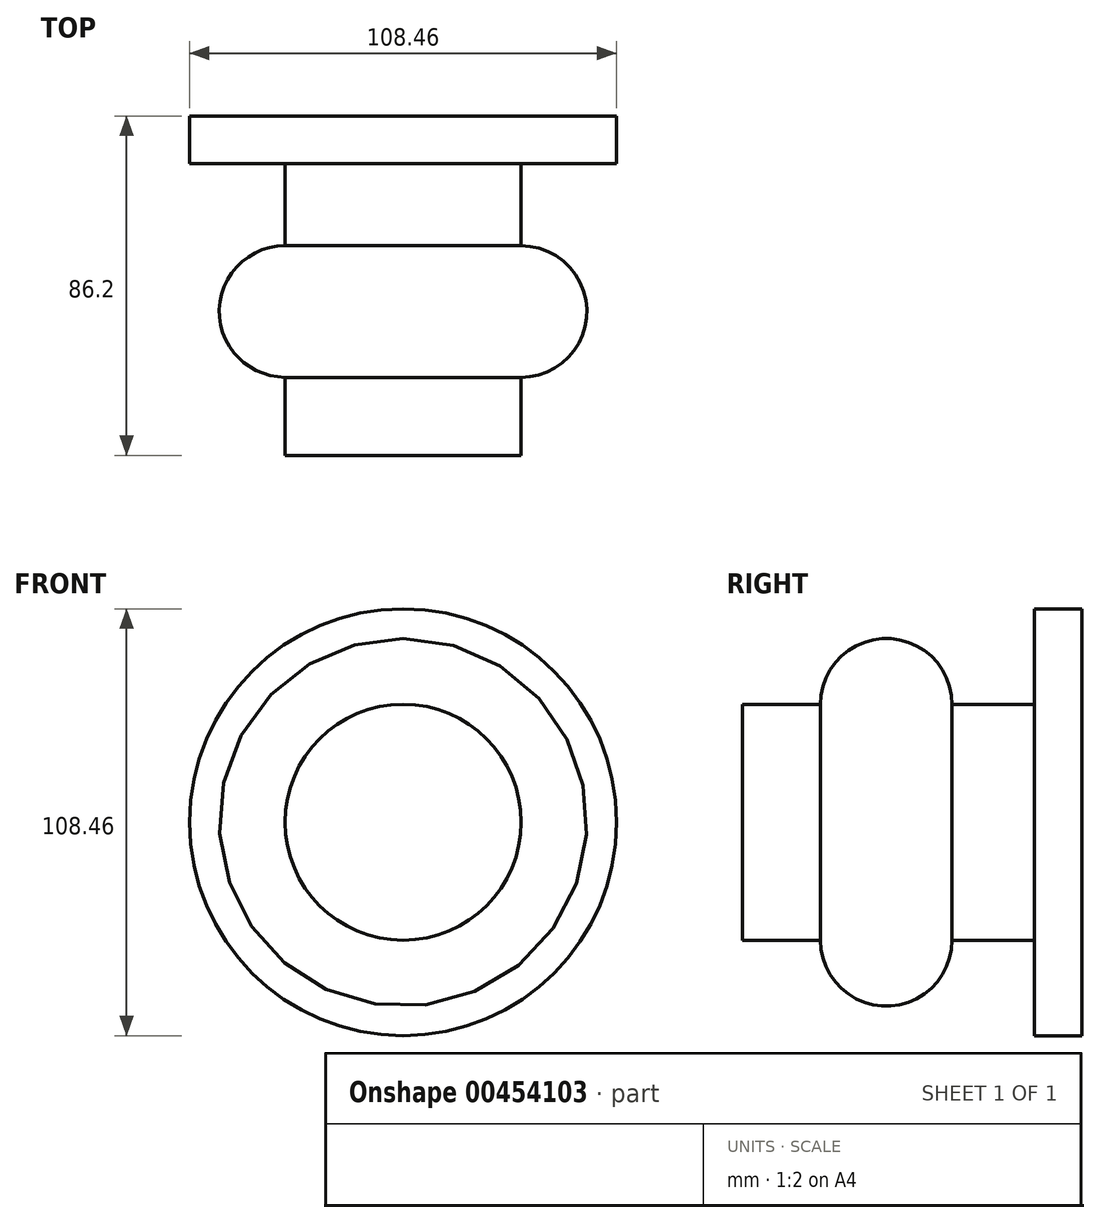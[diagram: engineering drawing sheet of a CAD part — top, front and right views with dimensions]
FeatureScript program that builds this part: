
annotation { "Feature Type Name" : "Feature", "Feature Type Description" : "" }
export const myFeature = defineFeature(function(context is Context, id is Id, definition is map)
    precondition{}
    {
        {
            var Q0;
            Q0=qCreatedBy(makeId("Top.planeOp"),FACE);
            var sketch = newSketch(context, id + "F0", { "sketchPlane" : qUnion([Q0])});
            skLineSegment(sketch, "E0", {"start": v(0, 40.66) * mm, "end": v(-54.23, 40.66) * mm});
            skLineSegment(sketch, "E1", {"start": v(-54.23, 40.66) * mm, "end": v(-54.23, 28.58) * mm});
            skLineSegment(sketch, "E2", {"start": v(-54.23, 28.58) * mm, "end": v(-29.98, 28.58) * mm});
            skLineSegment(sketch, "E3", {"start": v(-29.98, 28.58) * mm, "end": v(-29.98, 7.7) * mm});
            skLineSegment(sketch, "E4", {"start": v(-29.98, -25.73) * mm, "end": v(-29.98, -45.54) * mm});
            skLineSegment(sketch, "E5", {"start": v(-29.98, -45.54) * mm, "end": v(0, -45.54) * mm});
            skLineSegment(sketch, "E6", {"start": v(0, 40.66) * mm, "end": v(0, -45.54) * mm});
            skArc(sketch, "E7", {"start": v(-29.98, 7.7) * mm, "mid": v(-46.7, -9.01) * mm, "end": v(-29.98, -25.73) * mm});
            skSolve(sketch);
        }
        {
            var Q0;
            Q0 = qSketchRegion(id + "F0", true);
            var Q1;
            Q1=sQuery(id+"F0.wireOp",EDGE,"E6");
            revolve(context, id + "F1", {"entities" : qUnion([Q0]), "axis" : qUnion([Q1]), "revolveType" : RevolveType.FULL});
        }
    });
